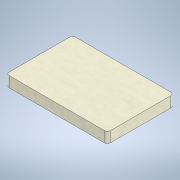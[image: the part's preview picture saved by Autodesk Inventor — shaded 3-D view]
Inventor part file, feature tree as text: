
AUTODESK INVENTOR PART (.ipt)
format: ipt  version: 2021 (Build 250183000, 183)  size: 111,616 bytes
history: native  units: mm
features: extrude x1, sketch x1
ambient origin geometry x8: Origin, YZ Plane, XZ Plane, XY Plane, X Axis, Y Axis, Z Axis, Center Point
bodies: Solid1 (feature_tree)
feature tree (2):
  extrude  "Extrusion1"  Depth=42.0mm
  sketch  "Sketch1"  dims[d0=64.0mm d1=42.0mm d2=2.0mm d3=6.7mm d4=0.0mm]
